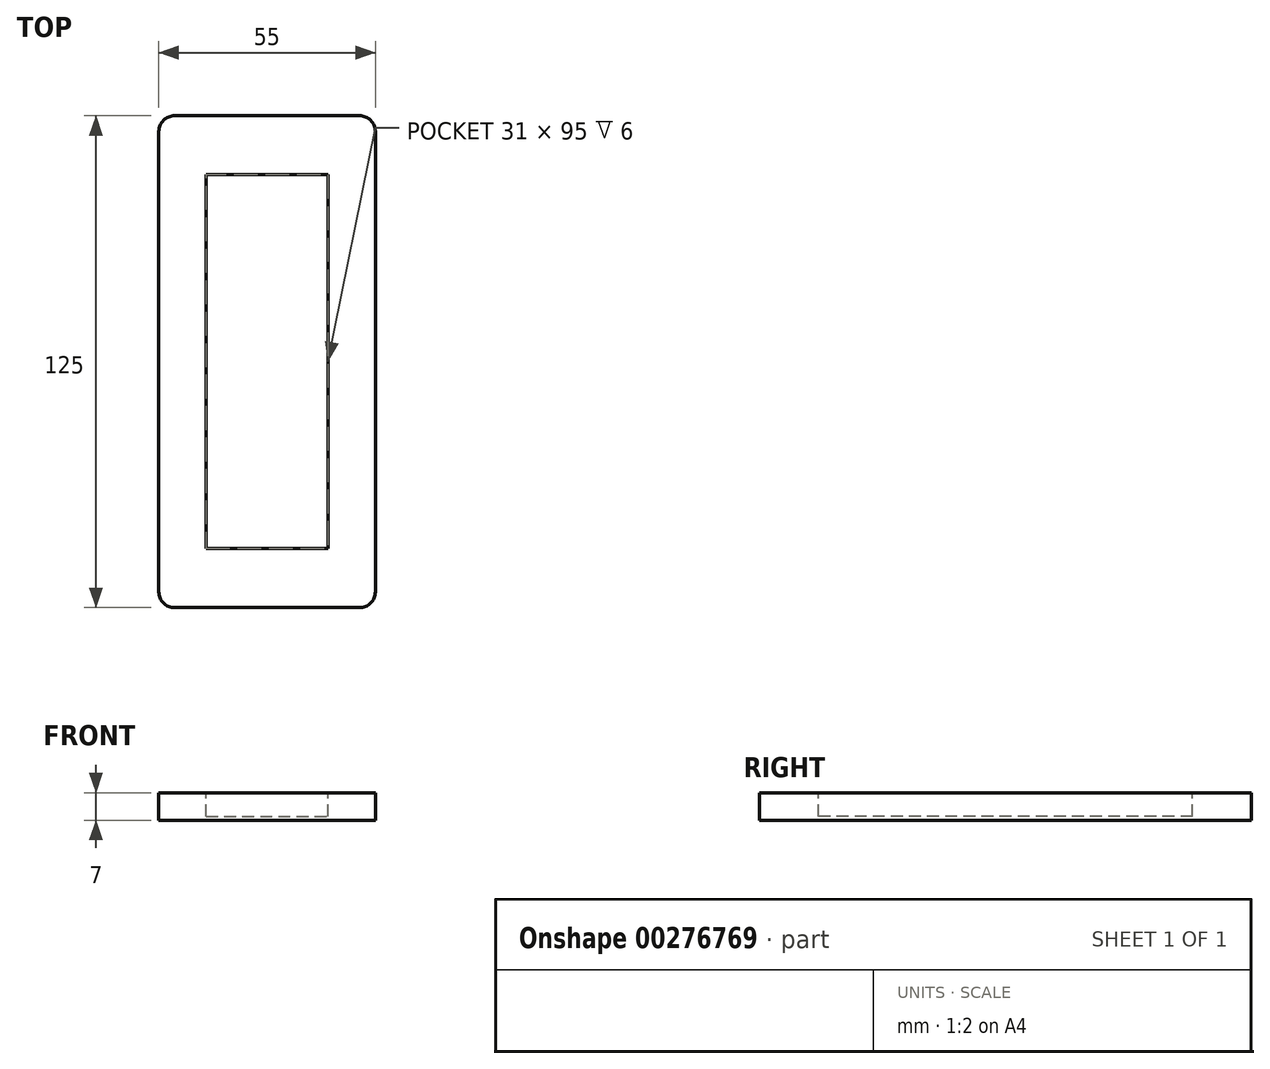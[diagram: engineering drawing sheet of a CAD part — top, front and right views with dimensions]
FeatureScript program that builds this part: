
annotation { "Feature Type Name" : "Feature", "Feature Type Description" : "" }
export const myFeature = defineFeature(function(context is Context, id is Id, definition is map)
    precondition{}
    {
        {
            var Q0;
            Q0=qCreatedBy(makeId("Top.planeOp"),FACE);
            var sketch = newSketch(context, id + "F0", { "sketchPlane" : qUnion([Q0])});
            skLineSegment(sketch, "E0.bottom", {"start": v(-23.5, 62.5) * mm, "end": v(23.5, 62.5) * mm});
            skLineSegment(sketch, "E0.top", {"start": v(-23.5, -62.5) * mm, "end": v(23.5, -62.5) * mm});
            skLineSegment(sketch, "E0.left", {"start": v(-27.5, 58.5) * mm, "end": v(-27.5, -58.5) * mm});
            skLineSegment(sketch, "E0.right", {"start": v(27.5, 58.5) * mm, "end": v(27.5, -58.5) * mm});
            skPoint(sketch, "E0.middle", {"position": v(0, 0) * mm});
            skPoint(sketch, "E1.visualSharp", {"position": v(-27.5, 62.5) * mm});
            skArc(sketch, "E1.filletArc", {"start": v(-23.5, 62.5) * mm, "mid": v(-26.33, 61.33) * mm, "end": v(-27.5, 58.5) * mm});
            skPoint(sketch, "E2.visualSharp", {"position": v(27.5, 62.5) * mm});
            skArc(sketch, "E2.filletArc", {"start": v(27.5, 58.5) * mm, "mid": v(26.33, 61.33) * mm, "end": v(23.5, 62.5) * mm});
            skPoint(sketch, "E3.visualSharp", {"position": v(27.5, -62.5) * mm});
            skArc(sketch, "E3.filletArc", {"start": v(23.5, -62.5) * mm, "mid": v(26.33, -61.33) * mm, "end": v(27.5, -58.5) * mm});
            skPoint(sketch, "E4.visualSharp", {"position": v(-27.5, -62.5) * mm});
            skArc(sketch, "E4.filletArc", {"start": v(-27.5, -58.5) * mm, "mid": v(-26.33, -61.33) * mm, "end": v(-23.5, -62.5) * mm});
            skSolve(sketch);
        }
        {
            var Q0;
            Q0=makeQuery(id+"F0.imprint","IMPRINT",FACE,{"disambiguationData":[TD([[makeQuery(id+"F0.imprint","IMPRINT",EDGE,{"derivedFrom":sQuery(id+"F0.wireOp",EDGE,"E0.bottom")}),-1.0]])]});
            extrude(context, id + "F1", {"entities" : qUnion([Q0]), "depth" : 7 * mm});
        }
        {
            var Q0;
            Q0=makeQuery(id+"F1.opExtrude","CAP_FACE",FACE,{"disambiguationData":[OSD([sQuery(id+"F0.wireOp",EDGE,"E0.bottom"),sQuery(id+"F0.wireOp",EDGE,"E0.top"),sQuery(id+"F0.wireOp",EDGE,"E0.left"),sQuery(id+"F0.wireOp",EDGE,"E0.right"),sQuery(id+"F0.wireOp",EDGE,"E1.filletArc"),sQuery(id+"F0.wireOp",EDGE,"E2.filletArc"),sQuery(id+"F0.wireOp",EDGE,"E3.filletArc"),sQuery(id+"F0.wireOp",EDGE,"E4.filletArc")])],"isStart":false});
            var sketch = newSketch(context, id + "F2", { "sketchPlane" : qUnion([Q0])});
            skLineSegment(sketch, "E5.bottom", {"start": v(-15.5, 47.5) * mm, "end": v(15.5, 47.5) * mm});
            skLineSegment(sketch, "E5.top", {"start": v(-15.5, -47.5) * mm, "end": v(15.5, -47.5) * mm});
            skLineSegment(sketch, "E5.left", {"start": v(-15.5, 47.5) * mm, "end": v(-15.5, -47.5) * mm});
            skLineSegment(sketch, "E5.right", {"start": v(15.5, 47.5) * mm, "end": v(15.5, -47.5) * mm});
            skPoint(sketch, "E5.middle", {"position": v(0, 0) * mm});
            skSolve(sketch);
        }
        {
            var Q0;
            Q0 = qSketchRegion(id + "F2", true);
            extrude(context, id + "F3", {"entities" : qUnion([Q0]), "operationType" : NewBodyOperationType.REMOVE, "oppositeDirection" : true, "depth" : 6 * mm});
        }
    });
